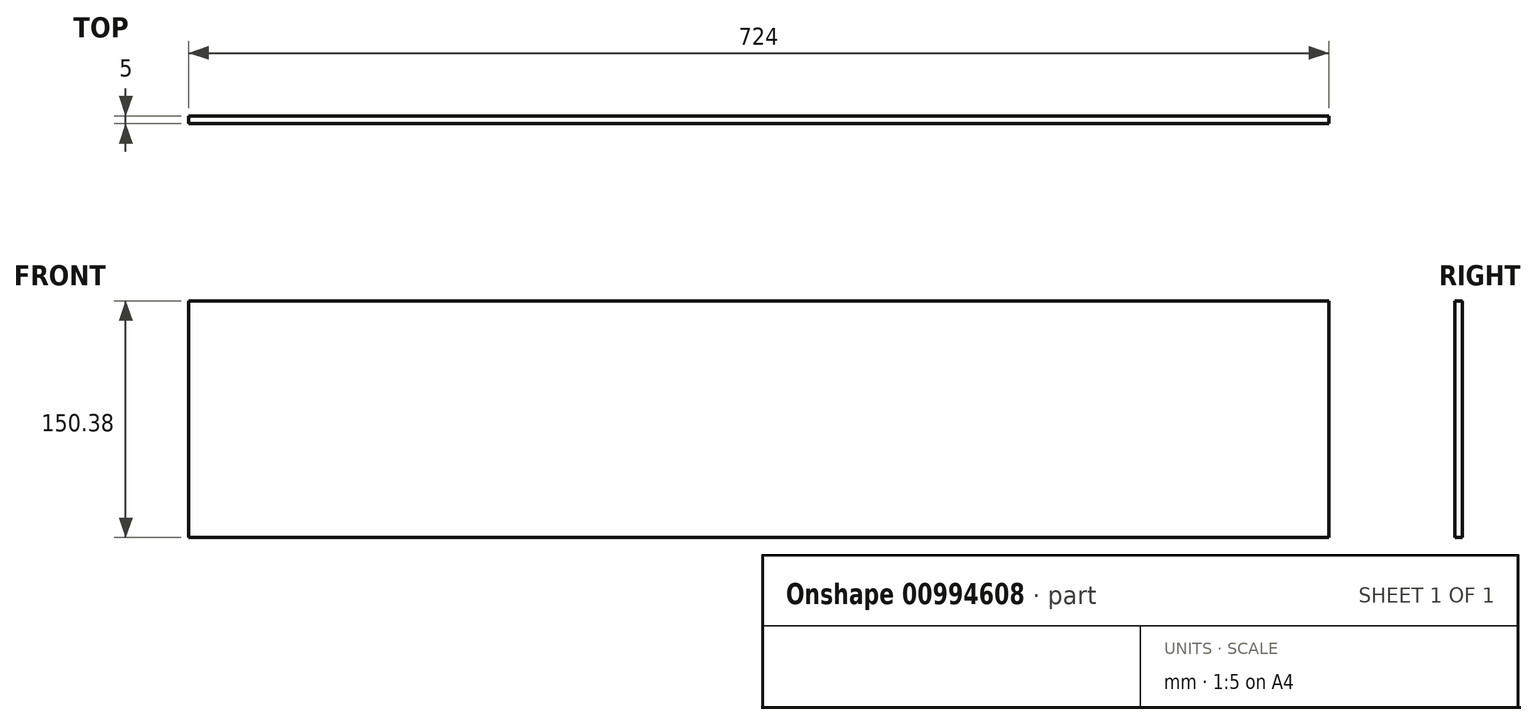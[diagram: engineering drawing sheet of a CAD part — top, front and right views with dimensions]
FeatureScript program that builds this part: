
annotation { "Feature Type Name" : "Feature", "Feature Type Description" : "" }
export const myFeature = defineFeature(function(context is Context, id is Id, definition is map)
    precondition{}
    {
        {
            var Q0;
            Q0=qCreatedBy(makeId("Front.planeOp"),FACE);
            var sketch = newSketch(context, id + "F0", { "sketchPlane" : qUnion([Q0])});
            skLineSegment(sketch, "E0.bottom", {"start": v(-362, -75.2) * mm, "end": v(362, -75.2) * mm});
            skLineSegment(sketch, "E0.top", {"start": v(-362, 75.2) * mm, "end": v(362, 75.2) * mm});
            skLineSegment(sketch, "E0.left", {"start": v(-362, -75.2) * mm, "end": v(-362, 75.2) * mm});
            skLineSegment(sketch, "E0.right", {"start": v(362, -75.2) * mm, "end": v(362, 75.2) * mm});
            skPoint(sketch, "E0.middle", {"position": v(0, 0) * mm});
            skSolve(sketch);
        }
        {
            var Q0;
            Q0=makeQuery(id+"F0.imprint","IMPRINT",FACE,{"disambiguationData":[TD([[makeQuery(id+"F0.imprint","IMPRINT",EDGE,{"derivedFrom":sQuery(id+"F0.wireOp",EDGE,"E0.bottom")}),1.0]])]});
            extrude(context, id + "F1", {"entities" : qUnion([Q0]), "depth" : 5 * mm, "offsetDistance" : 25 * mm});
        }
    });
